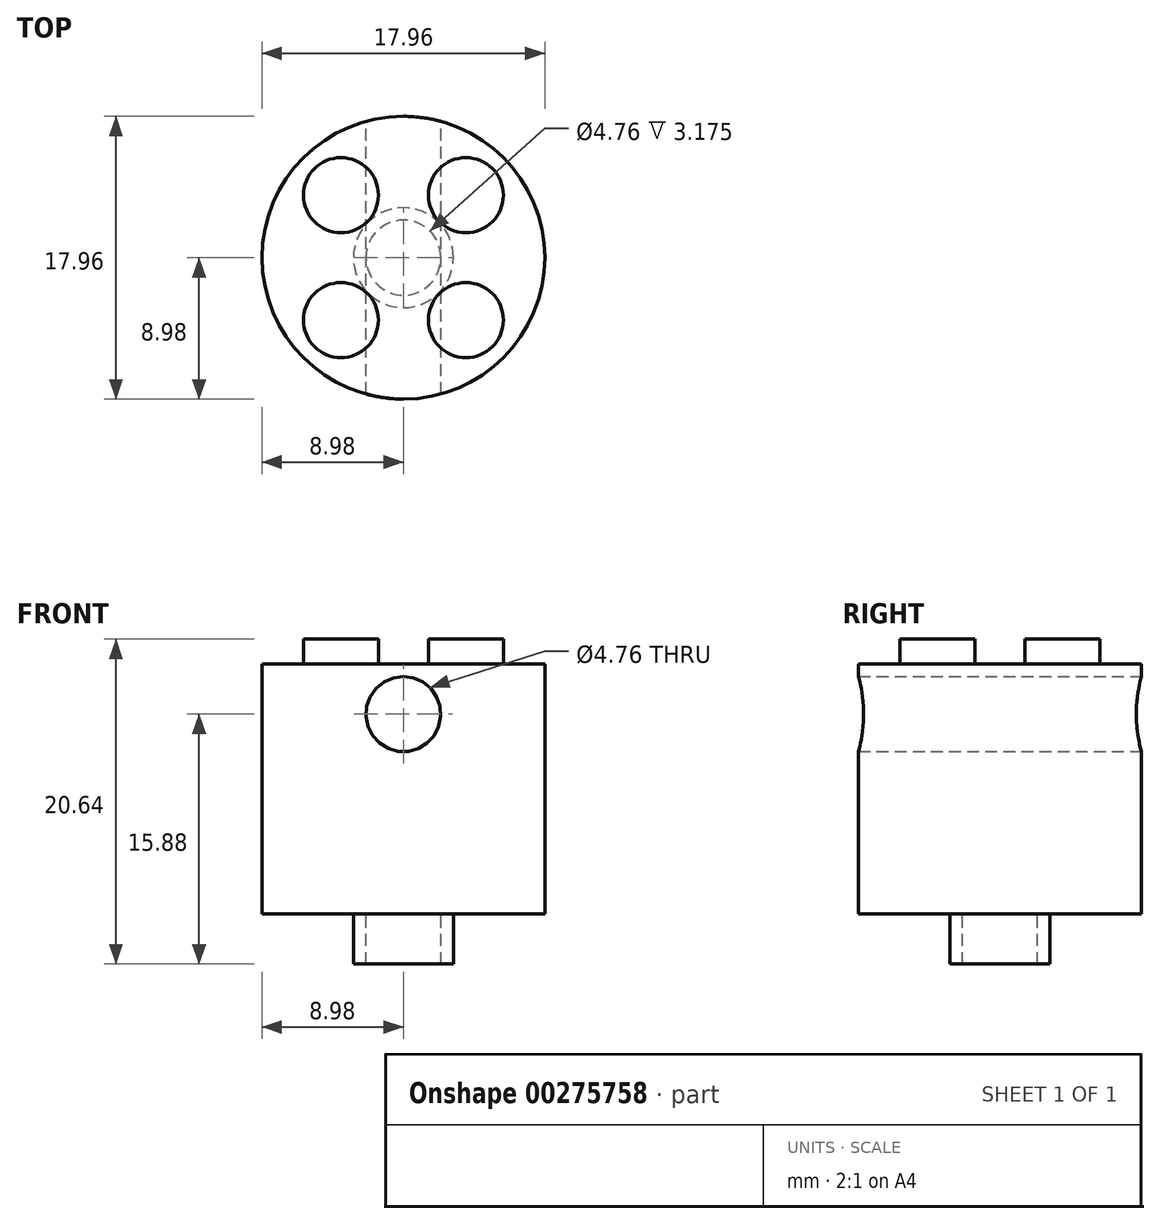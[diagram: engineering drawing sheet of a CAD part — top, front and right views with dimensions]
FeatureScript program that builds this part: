
annotation { "Feature Type Name" : "Feature", "Feature Type Description" : "" }
export const myFeature = defineFeature(function(context is Context, id is Id, definition is map)
    precondition{}
    {
        {
            var Q0;
            Q0=qCreatedBy(makeId("Top.planeOp"),FACE);
            var sketch = newSketch(context, id + "F0", { "sketchPlane" : qUnion([Q0])});
            skPoint(sketch, "E0.middle", {"position": v(0, 0) * mm});
            skCircle(sketch, "E1", {"center": v(0, 0) * mm, "radius": 8.98 * mm});
            skSolve(sketch);
        }
        {
            var Q0;
            Q0=makeQuery(id+"F0.imprint","IMPRINT",FACE,{"disambiguationData":[TD([[makeQuery(id+"F0.imprint","IMPRINT",EDGE,{"derivedFrom":sQuery(id+"F0.wireOp",EDGE,"E1")}),1.0]])]});
            extrude(context, id + "F1", {"entities" : qUnion([Q0]), "depth" : 15.88 * mm});
        }
        {
            var Q0;
            Q0=makeQuery(id+"F1.opExtrude","CAP_FACE",FACE,{"disambiguationData":[OSD([sQuery(id+"F0.wireOp",EDGE,"E1")])],"isStart":true});
            var sketch = newSketch(context, id + "F2", { "sketchPlane" : qUnion([Q0])});
            skCircle(sketch, "E2", {"center": v(0, 0) * mm, "radius": 3.18 * mm});
            skCircle(sketch, "E3.0", {"center": v(0, 0) * mm, "radius": 2.38 * mm});
            skSolve(sketch);
        }
        {
            var Q0;
            Q0=qSketchRegion(id+"F2",true);
            extrude(context, id + "F3", {"entities" : qUnion([Q0]), "operationType" : NewBodyOperationType.ADD, "depth" : 3.17 * mm});
        }
        {
            var Q0;
            Q0=makeQuery(id+"F1.opExtrude","CAP_FACE",FACE,{"disambiguationData":[OSD([sQuery(id+"F0.wireOp",EDGE,"E1")])],"isStart":false});
            var sketch = newSketch(context, id + "F4", { "sketchPlane" : qUnion([Q0])});
            skLineSegment(sketch, "E4", {"start": v(0, 0) * mm, "end": v(0, 8.98) * mm});
            skLineSegment(sketch, "E5", {"start": v(0, 0) * mm, "end": v(0, -8.98) * mm});
            skLineSegment(sketch, "E6", {"start": v(0, 0) * mm, "end": v(8.98, 0) * mm});
            skLineSegment(sketch, "E7", {"start": v(0, 0) * mm, "end": v(-8.98, 0) * mm});
            skPoint(sketch, "E8", {"position": v(-3.97, 0) * mm});
            skPoint(sketch, "E9", {"position": v(0, -3.97) * mm});
            skPoint(sketch, "E10.MirrorP", {"position": v(3.97, 0) * mm});
            skPoint(sketch, "E11.MirrorP", {"position": v(0, 3.97) * mm});
            skCircle(sketch, "E12", {"center": v(-3.97, 3.97) * mm, "radius": 2.38 * mm});
            skCircle(sketch, "E13", {"center": v(3.97, 3.97) * mm, "radius": 2.38 * mm});
            skCircle(sketch, "E14.MirrorC", {"center": v(3.97, -3.97) * mm, "radius": 2.38 * mm});
            skCircle(sketch, "E15.MirrorC", {"center": v(-3.97, -3.97) * mm, "radius": 2.38 * mm});
            skSolve(sketch);
        }
        {
            var Q0;
            Q0=qSketchRegion(id+"F4",true);
            extrude(context, id + "F5", {"entities" : qUnion([Q0]), "operationType" : NewBodyOperationType.ADD, "depth" : 1.59 * mm});
        }
        {
            var Q0;
            Q0=qCreatedBy(makeId("Front.planeOp"),FACE);
            var sketch = newSketch(context, id + "F6", { "sketchPlane" : qUnion([Q0])});
            skLineSegment(sketch, "E16", {"start": v(0, 0) * mm, "end": v(0, 12.7) * mm});
            skCircle(sketch, "E17", {"center": v(0, 12.7) * mm, "radius": 2.38 * mm});
            skSolve(sketch);
        }
        {
            var Q0;
            Q0=qSketchRegion(id+"F6",true);
            extrude(context, id + "F7", {"entities" : qUnion([Q0]), "operationType" : NewBodyOperationType.REMOVE, "endBound" : BoundingType.SYMMETRIC, "depth" : 25.4 * mm});
        }
    });
